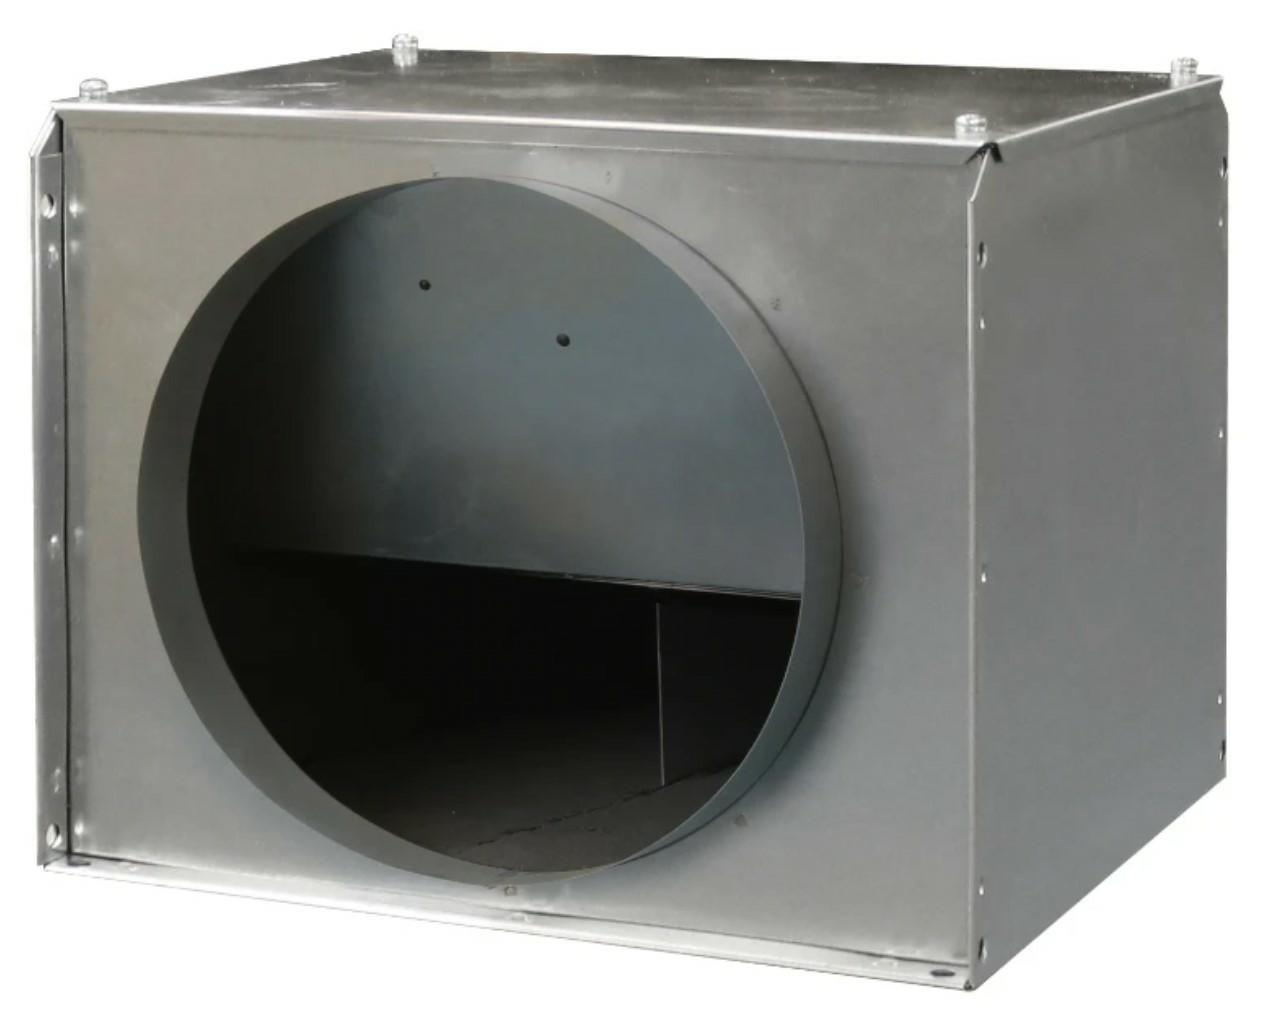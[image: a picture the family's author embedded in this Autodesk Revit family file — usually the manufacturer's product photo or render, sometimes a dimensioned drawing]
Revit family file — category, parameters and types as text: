
# Revit family: CADS_Vent-Axia_MechEquip_Fan_QP_QuietPackAcoustic - EXTRACT
name_source: partatom
category: Mechanical Equipment
units: mm (PartAtom-declared; Revit-internal decimal feet)

## family parameters
Classification = None
Cut with Voids When Loaded = No
Host = Face
OmniClass Number = 23.75.35.17.11
OmniClass Title = Fans for Air Ductwork
Part Type = Normal
Room Calculation Point = No
Round Connector Dimension = Use Diameter
Shared = No

## types (9) — shared parameters
AirflowRateRange = 0.0 L/s
AssemblyPlace = UNKNOWN
AssetType = FIXED
Default Elevation = 1219 mm
DurationUnit = Year
EBHoffset = 110 mm
EBVoffset = 55 mm
ExteriorInsulation = No
Fitting Type = Ignore
GrossWeight = 0.00 kg
HasProtectiveEarth = No
IsExtendedWarranty = No
ManufacturerAddress = Fleming Way
Crawley 
RH10 9YX
Quantity = 1
RatedCurrent = 0 A
RatedVoltage = 0 V
Status = New
WarrantyGuarantor = Vent-Axia Limited
WorkingPressure = 0.0 Pa
zero-valued in all types: CADS_Index, CADS_Usage, ExpectedServiceLife, H, NumberOfPoles, W

## per-type parameters (varying)
| type | L | ModelReference | NominalDiameter | NominalHeight | NominalLength | NominalWidth | OutOffset | OverallLength | SpigotCLHeight | SpigotLength | Type Image |
| QP100C | 360 mm | ACOUSTIC BOX FAN, 100 DIA SPIGOTS | 100 mm  [stored 0.328084 ft] | 190 mm | 400 mm | 310 mm | 111 mm | 460 mm | 94 mm | 30 mm  [stored 0.0984252 ft] | <None> |
| QP125C | 360 mm | ACOUSTIC BOX FAN, 125 DIA SPIGOTS | 125 mm  [stored 0.410105 ft] | 190 mm | 400 mm | 310 mm | 111 mm | 460 mm | 94 mm | 30 mm  [stored 0.0984252 ft] | <None> |
| QP150C | 360 mm | ACOUSTIC BOX FAN, 150 DIA SPIGOTS | 150 mm | 190 mm | 400 mm | 310 mm | 111 mm | 460 mm | 94 mm | 30 mm  [stored 0.0984252 ft] | <None> |
| QP160C | 360 mm | ACOUSTIC BOX FAN, 160 DIA SPIGOTS | 160 mm | 190 mm | 400 mm | 310 mm | 111 mm | 460 mm | 94 mm | 30 mm  [stored 0.0984252 ft] | <None> |
| QP200C | 415 mm | ACOUSTIC BOX FAN, 200 DIA SPIGOTS | 200 mm  [stored 0.656168 ft] | 285 mm | 455 mm | 364 mm | 127 mm | 515 mm | 141 mm | 30 mm  [stored 0.0984252 ft] | <None> |
| QP250C | 415 mm | ACOUSTIC BOX FAN, 250 DIA SPIGOTS | 250 mm  [stored 0.82021 ft] | 285 mm | 455 mm | 364 mm | 127 mm | 515 mm | 141 mm | 30 mm  [stored 0.0984252 ft] | <None> |
| QP315C | 690 mm | ACOUSTIC BOX FAN,315 DIA SPIGOTS | 315 mm | 456 mm | 730 mm | 572 mm | 243 mm | 792 mm | 227 mm | 31 mm | <None> |
| QP400C | 690 mm | ACOUSTIC BOX FAN, 400 DIA SPIGOTS | 400 mm | 456 mm | 730 mm | 572 mm | 243 mm | 792 mm | 227 mm | 31 mm | <None> |
| QP500C | 878 mm  [stored 2.88058 ft] | ACOUSTIC BOX FAN, 500 DIA SPIGOTS | 500 mm  [stored 1.64042 ft] | 575 mm  [stored 1.88648 ft] | 918 mm | 769 mm  [stored 2.52297 ft] | 326 mm  [stored 1.06955 ft] | 1006 mm | 286 mm | 44 mm | CADS_Vent-Axia_MechEquip_Fan_QP_QuietPackAcoustic.jpg |

note: column(s) folded — value = type name in every type: ModelNumber

note: [stored X ft] marks values corroborated as IEEE doubles in the binary element streams (Revit-internal decimal feet)

## geometry (parser evidence)
native form markers: Sweep x5
no freeform markers — native parametric forms only
